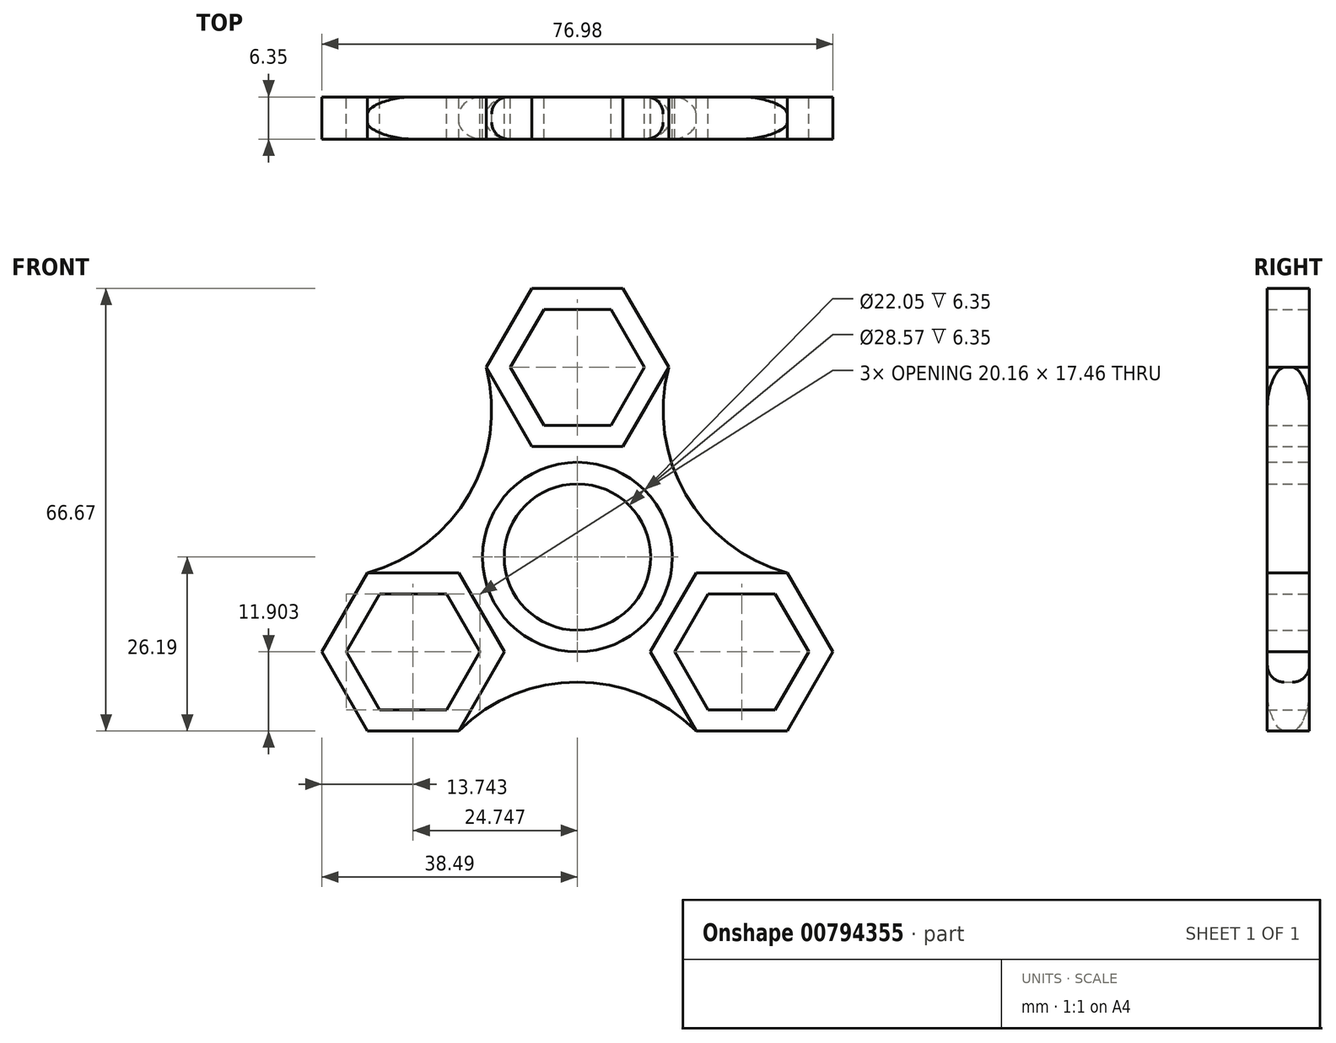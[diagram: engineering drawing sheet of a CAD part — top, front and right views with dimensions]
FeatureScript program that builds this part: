
annotation { "Feature Type Name" : "Feature", "Feature Type Description" : "" }
export const myFeature = defineFeature(function(context is Context, id is Id, definition is map)
    precondition{}
    {
        {
            var Q0;
            Q0=qCreatedBy(makeId("Front.planeOp"),FACE);
            var sketch = newSketch(context, id + "F0", { "sketchPlane" : qUnion([Q0])});
            skCircle(sketch, "E0", {"center": v(0, 0) * mm, "radius": 14.29 * mm});
            skCircle(sketch, "E1", {"center": v(0, 0) * mm, "radius": 11.02 * mm});
            skCircle(sketch, "E2.cCircle", {"center": v(0, 28.58) * mm, "radius": 11.9 * mm, "construction": true});
            skLineSegment(sketch, "E2.0", {"start": v(-6.87, 40.48) * mm, "end": v(6.87, 40.48) * mm});
            skLineSegment(sketch, "E2.1", {"start": v(6.87, 40.48) * mm, "end": v(13.75, 28.58) * mm});
            skLineSegment(sketch, "E2.2", {"start": v(13.75, 28.58) * mm, "end": v(6.87, 16.67) * mm});
            skLineSegment(sketch, "E2.3", {"start": v(6.87, 16.67) * mm, "end": v(-6.87, 16.67) * mm});
            skLineSegment(sketch, "E2.4", {"start": v(-6.87, 16.67) * mm, "end": v(-13.75, 28.58) * mm});
            skLineSegment(sketch, "E2.5", {"start": v(-13.75, 28.58) * mm, "end": v(-6.87, 40.48) * mm});
            skPoint(sketch, "E2.0.midPoint", {"position": v(0, 40.48) * mm});
            skCircle(sketch, "E3.cCircle", {"center": v(0, 28.58) * mm, "radius": 8.73 * mm, "construction": true});
            skLineSegment(sketch, "E3.0", {"start": v(5.04, 19.84) * mm, "end": v(-5.04, 19.84) * mm});
            skLineSegment(sketch, "E3.1", {"start": v(-5.04, 19.84) * mm, "end": v(-10.08, 28.57) * mm});
            skLineSegment(sketch, "E3.2", {"start": v(-10.08, 28.57) * mm, "end": v(-5.04, 37.3) * mm});
            skLineSegment(sketch, "E3.3", {"start": v(-5.04, 37.3) * mm, "end": v(5.04, 37.3) * mm});
            skLineSegment(sketch, "E3.4", {"start": v(5.04, 37.3) * mm, "end": v(10.08, 28.58) * mm});
            skLineSegment(sketch, "E3.5", {"start": v(10.08, 28.58) * mm, "end": v(5.04, 19.84) * mm});
            skPoint(sketch, "E3.0.midPoint", {"position": v(0, 19.84) * mm});
            skLineSegment(sketch, "E4.1.0", {"start": v(-19.7, -23.02) * mm, "end": v(-29.79, -23.02) * mm});
            skPoint(sketch, "E4.1.1", {"position": v(-17.19, -9.92) * mm});
            skCircle(sketch, "E4.1.2", {"center": v(-24.75, -14.29) * mm, "radius": 8.73 * mm, "construction": true});
            skLineSegment(sketch, "E4.1.3", {"start": v(-17.87, -2.38) * mm, "end": v(-11, -14.29) * mm});
            skLineSegment(sketch, "E4.1.4", {"start": v(-38.5, -14.29) * mm, "end": v(-31.62, -2.38) * mm});
            skLineSegment(sketch, "E4.1.5", {"start": v(-29.79, -5.56) * mm, "end": v(-19.7, -5.56) * mm});
            skLineSegment(sketch, "E4.1.6", {"start": v(-34.83, -14.29) * mm, "end": v(-29.79, -5.56) * mm});
            skLineSegment(sketch, "E4.1.7", {"start": v(-31.62, -2.38) * mm, "end": v(-17.87, -2.38) * mm});
            skLineSegment(sketch, "E4.1.8", {"start": v(-11, -14.29) * mm, "end": v(-17.87, -26.2) * mm});
            skLineSegment(sketch, "E4.1.9", {"start": v(-17.87, -26.2) * mm, "end": v(-31.62, -26.2) * mm});
            skCircle(sketch, "E4.1.10", {"center": v(-24.75, -14.29) * mm, "radius": 11.9 * mm, "construction": true});
            skLineSegment(sketch, "E4.1.11", {"start": v(-31.62, -26.2) * mm, "end": v(-38.5, -14.29) * mm});
            skPoint(sketch, "E4.1.12", {"position": v(-35.06, -20.24) * mm});
            skLineSegment(sketch, "E4.1.13", {"start": v(-29.79, -23.02) * mm, "end": v(-34.83, -14.29) * mm});
            skLineSegment(sketch, "E4.1.14", {"start": v(-19.7, -5.56) * mm, "end": v(-14.66, -14.29) * mm});
            skLineSegment(sketch, "E4.1.15", {"start": v(-14.66, -14.29) * mm, "end": v(-19.7, -23.02) * mm});
            skLineSegment(sketch, "E4.2.0", {"start": v(29.79, -5.56) * mm, "end": v(34.83, -14.29) * mm});
            skPoint(sketch, "E4.2.1", {"position": v(17.19, -9.92) * mm});
            skCircle(sketch, "E4.2.2", {"center": v(24.75, -14.29) * mm, "radius": 8.73 * mm, "construction": true});
            skLineSegment(sketch, "E4.2.3", {"start": v(11, -14.29) * mm, "end": v(17.87, -2.38) * mm});
            skLineSegment(sketch, "E4.2.4", {"start": v(31.62, -26.2) * mm, "end": v(17.87, -26.2) * mm});
            skLineSegment(sketch, "E4.2.5", {"start": v(19.7, -23.02) * mm, "end": v(14.66, -14.29) * mm});
            skLineSegment(sketch, "E4.2.6", {"start": v(29.79, -23.02) * mm, "end": v(19.7, -23.02) * mm});
            skLineSegment(sketch, "E4.2.7", {"start": v(17.87, -26.2) * mm, "end": v(11, -14.29) * mm});
            skLineSegment(sketch, "E4.2.8", {"start": v(17.87, -2.38) * mm, "end": v(31.62, -2.38) * mm});
            skLineSegment(sketch, "E4.2.9", {"start": v(31.62, -2.38) * mm, "end": v(38.5, -14.29) * mm});
            skCircle(sketch, "E4.2.10", {"center": v(24.75, -14.29) * mm, "radius": 11.9 * mm, "construction": true});
            skLineSegment(sketch, "E4.2.11", {"start": v(38.5, -14.29) * mm, "end": v(31.62, -26.2) * mm});
            skPoint(sketch, "E4.2.12", {"position": v(35.06, -20.24) * mm});
            skLineSegment(sketch, "E4.2.13", {"start": v(34.83, -14.29) * mm, "end": v(29.79, -23.02) * mm});
            skLineSegment(sketch, "E4.2.14", {"start": v(14.66, -14.29) * mm, "end": v(19.7, -5.56) * mm});
            skLineSegment(sketch, "E4.2.15", {"start": v(19.7, -5.56) * mm, "end": v(29.79, -5.56) * mm});
            skSolve(sketch);
        }
        {
            var Q0;
            Q0=qCreatedBy(makeId("Front.planeOp"),FACE);
            var sketch = newSketch(context, id + "F1", { "sketchPlane" : qUnion([Q0])});
            skCircle(sketch, "E5.0", {"center": v(24.75, -14.29) * mm, "radius": 11.9 * mm});
            skLineSegment(sketch, "E5.1", {"start": v(13.75, 28.58) * mm, "end": v(6.87, 16.67) * mm});
            skCircle(sketch, "E5.2", {"center": v(-24.75, -14.29) * mm, "radius": 8.73 * mm});
            skLineSegment(sketch, "E5.3", {"start": v(6.87, 40.48) * mm, "end": v(13.75, 28.58) * mm});
            skCircle(sketch, "E5.4", {"center": v(0, 28.58) * mm, "radius": 11.9 * mm});
            skLineSegment(sketch, "E5.5", {"start": v(11, -14.29) * mm, "end": v(17.87, -2.38) * mm});
            skLineSegment(sketch, "E5.6", {"start": v(-6.87, 16.67) * mm, "end": v(-13.75, 28.58) * mm});
            skCircle(sketch, "E5.7", {"center": v(0, 28.58) * mm, "radius": 8.73 * mm});
            skCircle(sketch, "E5.8", {"center": v(-24.75, -14.29) * mm, "radius": 11.9 * mm});
            skCircle(sketch, "E5.9", {"center": v(0, 0) * mm, "radius": 11.02 * mm});
            skLineSegment(sketch, "E5.10", {"start": v(5.04, 19.84) * mm, "end": v(-5.04, 19.84) * mm});
            skLineSegment(sketch, "E5.11", {"start": v(-14.66, -14.29) * mm, "end": v(-19.7, -23.02) * mm});
            skLineSegment(sketch, "E5.12", {"start": v(-29.79, -23.02) * mm, "end": v(-34.83, -14.29) * mm});
            skLineSegment(sketch, "E5.13", {"start": v(-19.7, -5.56) * mm, "end": v(-14.66, -14.29) * mm});
            skLineSegment(sketch, "E5.14", {"start": v(31.62, -26.2) * mm, "end": v(17.87, -26.2) * mm});
            skLineSegment(sketch, "E5.15", {"start": v(29.79, -23.02) * mm, "end": v(19.7, -23.02) * mm});
            skLineSegment(sketch, "E5.16", {"start": v(17.87, -26.2) * mm, "end": v(11, -14.29) * mm});
            skLineSegment(sketch, "E5.17", {"start": v(-13.75, 28.58) * mm, "end": v(-6.87, 40.48) * mm});
            skLineSegment(sketch, "E5.18", {"start": v(6.87, 16.67) * mm, "end": v(-6.87, 16.67) * mm});
            skLineSegment(sketch, "E5.19", {"start": v(-6.87, 40.48) * mm, "end": v(6.87, 40.48) * mm});
            skLineSegment(sketch, "E5.20", {"start": v(29.79, -5.56) * mm, "end": v(34.83, -14.29) * mm});
            skLineSegment(sketch, "E5.21", {"start": v(19.7, -23.02) * mm, "end": v(14.66, -14.29) * mm});
            skLineSegment(sketch, "E5.22", {"start": v(17.87, -2.38) * mm, "end": v(31.62, -2.38) * mm});
            skCircle(sketch, "E5.23", {"center": v(24.75, -14.29) * mm, "radius": 8.73 * mm});
            skCircle(sketch, "E5.24", {"center": v(0, 0) * mm, "radius": 14.29 * mm});
            skLineSegment(sketch, "E5.25", {"start": v(-31.62, -26.2) * mm, "end": v(-38.5, -14.29) * mm});
            skLineSegment(sketch, "E5.26", {"start": v(-5.04, 19.84) * mm, "end": v(-10.08, 28.57) * mm});
            skLineSegment(sketch, "E5.27", {"start": v(31.62, -2.38) * mm, "end": v(38.5, -14.29) * mm});
            skLineSegment(sketch, "E5.28", {"start": v(19.7, -5.56) * mm, "end": v(29.79, -5.56) * mm});
            skLineSegment(sketch, "E5.29", {"start": v(-17.87, -26.2) * mm, "end": v(-31.62, -26.2) * mm});
            skLineSegment(sketch, "E5.30", {"start": v(-10.08, 28.57) * mm, "end": v(-5.04, 37.3) * mm});
            skLineSegment(sketch, "E5.31", {"start": v(14.66, -14.29) * mm, "end": v(19.7, -5.56) * mm});
            skLineSegment(sketch, "E5.32", {"start": v(-11, -14.29) * mm, "end": v(-17.87, -26.2) * mm});
            skLineSegment(sketch, "E5.33", {"start": v(-5.04, 37.3) * mm, "end": v(5.04, 37.3) * mm});
            skLineSegment(sketch, "E5.34", {"start": v(34.83, -14.29) * mm, "end": v(29.79, -23.02) * mm});
            skLineSegment(sketch, "E5.35", {"start": v(-31.62, -2.38) * mm, "end": v(-17.87, -2.38) * mm});
            skLineSegment(sketch, "E5.36", {"start": v(5.04, 37.3) * mm, "end": v(10.08, 28.58) * mm});
            skLineSegment(sketch, "E5.37", {"start": v(38.5, -14.29) * mm, "end": v(31.62, -26.2) * mm});
            skLineSegment(sketch, "E5.38", {"start": v(-34.83, -14.29) * mm, "end": v(-29.79, -5.56) * mm});
            skLineSegment(sketch, "E5.39", {"start": v(10.08, 28.58) * mm, "end": v(5.04, 19.84) * mm});
            skLineSegment(sketch, "E5.40", {"start": v(-19.7, -23.02) * mm, "end": v(-29.79, -23.02) * mm});
            skLineSegment(sketch, "E5.41", {"start": v(-29.79, -5.56) * mm, "end": v(-19.7, -5.56) * mm});
            skLineSegment(sketch, "E5.42", {"start": v(-17.87, -2.38) * mm, "end": v(-11, -14.29) * mm});
            skLineSegment(sketch, "E5.43", {"start": v(-38.5, -14.29) * mm, "end": v(-31.62, -2.38) * mm});
            skArc(sketch, "E6", {"start": v(-31.62, -2.38) * mm, "mid": v(-16.32, 9.42) * mm, "end": v(-13.75, 28.58) * mm});
            skArc(sketch, "E7.1.0", {"start": v(17.87, -26.2) * mm, "mid": v(0, -18.84) * mm, "end": v(-17.87, -26.2) * mm});
            skArc(sketch, "E7.2.0", {"start": v(13.75, 28.57) * mm, "mid": v(16.32, 9.42) * mm, "end": v(31.62, -2.38) * mm});
            skSolve(sketch);
        }
        {
            var Q0;
            Q0=makeQuery(id+"F1.imprint","IMPRINT",FACE,{"disambiguationData":[TD([[makeQuery(id+"F1.imprint","IMPRINT",EDGE,{"derivedFrom":sQuery(id+"F1.wireOp",EDGE,"E5.24")}),-1.0]])]});
            var Q1;
            Q1=makeQuery(id+"F0.imprint","IMPRINT",FACE,{"disambiguationData":[TD([[makeQuery(id+"F0.imprint","IMPRINT",EDGE,{"derivedFrom":sQuery(id+"F0.wireOp",EDGE,"E0")}),1.0]])]});
            var Q2;
            Q2=makeQuery(id+"F0.imprint","IMPRINT",FACE,{"disambiguationData":[TD([[makeQuery(id+"F0.imprint","IMPRINT",EDGE,{"derivedFrom":sQuery(id+"F0.wireOp",EDGE,"E4.1.0")}),1.0]])]});
            var Q3;
            Q3=makeQuery(id+"F0.imprint","IMPRINT",FACE,{"disambiguationData":[TD([[makeQuery(id+"F0.imprint","IMPRINT",EDGE,{"derivedFrom":sQuery(id+"F0.wireOp",EDGE,"E2.0")}),-1.0]])]});
            var Q4;
            Q4=makeQuery(id+"F0.imprint","IMPRINT",FACE,{"disambiguationData":[TD([[makeQuery(id+"F0.imprint","IMPRINT",EDGE,{"derivedFrom":sQuery(id+"F0.wireOp",EDGE,"E4.2.0")}),1.0]])]});
            extrude(context, id + "F2", {"entities" : qUnion([Q0, Q1, Q2, Q3, Q4]), "depth" : 6.35 * mm, "offsetDistance" : 25.4 * mm});
        }
        {
            var Q0;
            Q0=makeQuery(id+"F2.opExtrude","CAP_EDGE",EDGE,{"disambiguationData":[OSD([sQuery(id+"F1.wireOp",EDGE,"E7.2.0")])],"isStart":false});
            var Q1;
            Q1=makeQuery(id+"F2.opExtrude","CAP_EDGE",EDGE,{"disambiguationData":[OSD([sQuery(id+"F1.wireOp",EDGE,"E7.1.0")])],"isStart":false});
            var Q2;
            Q2=makeQuery(id+"F2.opExtrude","CAP_EDGE",EDGE,{"disambiguationData":[OSD([sQuery(id+"F1.wireOp",EDGE,"E7.1.0")])],"isStart":true});
            var Q3;
            Q3=makeQuery(id+"F2.opExtrude","CAP_EDGE",EDGE,{"disambiguationData":[OSD([sQuery(id+"F1.wireOp",EDGE,"E6")])],"isStart":true});
            var Q4;
            Q4=makeQuery(id+"F2.opExtrude","CAP_EDGE",EDGE,{"disambiguationData":[OSD([sQuery(id+"F1.wireOp",EDGE,"E6")])],"isStart":false});
            var Q5;
            Q5=makeQuery(id+"F2.opExtrude","CAP_EDGE",EDGE,{"disambiguationData":[OSD([sQuery(id+"F1.wireOp",EDGE,"E7.2.0")])],"isStart":true});
            fillet(context, id + "F3", {"entities" : qUnion([Q0, Q1, Q2, Q3, Q4, Q5]), "radius" : 2.54 * mm, "tangentPropagation" : true, "allowEdgeOverflow" : false});
        }
    });
